# Revit family: Переходник с внутренней резьбой
name_source: partatom
category: Соединительные детали трубопроводов
revit_build: Autodesk Revit 2017 (Build: 20160225_1515(x64)
units: mm (PartAtom-declared; Revit-internal decimal feet)

## family parameters
Всегда вертикально = Да
На основе рабочей плоскости = Нет
Общий = Нет
При загрузке вырезать с полостями = Нет
Размер круглого соединителя = Использовать радиус
Тип детали = Соединение

## types (7) — shared parameters
ADSK_Единица измерения = шт
ADSK_Завод-изготовитель = Sanext
URL = http://sanext.ru
Изготовитель = Sanext
Материал фитинга = DZR латунь
Разработчик = ООО ПРОРУБИМ
Разработчик (телефон) = +7(495)649-85-43
Разработчик модели (URL) = http://prorubim.com
zero-valued in all types: ADSK_Масса

## per-type parameters (varying)
| type | ADSK_Код изделия | D1 | DN | G | G/2 | R | S | a | Лево | Право |
| Переходник с внутренней резбой 32xG1" | 4142 | 37 мм | 32 мм | 32 мм | 16 мм | 16 мм | 37 мм | 71 мм | Нет | Да |
| Переходник с внутренней резбой 32xG3/4" | 4141 | 37 мм | 32 мм | 25 мм | 13 мм | 16 мм | 37 мм | 69 мм | Да | Нет |
| Переходник с внутренней резбой 25xG1" | 4132 | 37 мм | 25 мм | 32 мм | 16 мм | 13 мм | 37 мм | 66 мм | Нет | Да |
| Переходник с внутренней резбой 25xG3/4" | 4131 | 30 мм | 25 мм | 25 мм | 13 мм | 13 мм | 30 мм | 63 мм | Нет | Да |
| Переходник с внутренней резбой 20xG3/4" | 4121 | 30 мм | 20 мм | 25 мм | 13 мм | 10 мм | 30 мм | 57 мм | Нет | Да |
| Переходник с внутренней резбой 20xG1/2'' | 4120 | 25 мм | 20 мм | 20 мм | 10 мм | 10 мм | 25 мм | 54 мм | Нет | Да |
| Переходник с внутренней резбой 16xG1/2'' | 4110 | 25 мм | 16 мм | 20 мм | 10 мм | 8 мм | 25 мм | 49 мм | Нет | Да |

note: column(s) folded — value = type name in every type: ADSK_Наименование
